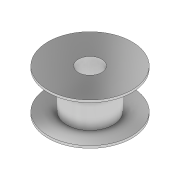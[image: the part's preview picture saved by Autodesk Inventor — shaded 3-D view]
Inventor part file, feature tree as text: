
AUTODESK INVENTOR PART (.ipt)
format: ipt  version: 2020 (Build 240168000, 168)  size: 109,056 bytes
history: native  units: in
note: dims shown in document units (in); Inventor stores cm internally (conversion verified against a paired STEP export)
features: extrude x3, sketch x3
ambient origin geometry x8: Origin, YZ Plane, XZ Plane, XY Plane, X Axis, Y Axis, Z Axis, Center Point
bodies: Solid1 (feature_tree)
feature tree (6):
  extrude  "Extrusion1"  Depth=0.1969in
  extrude  "Extrusion2"  Depth=0.3937in
  extrude  "Extrusion3"  Depth=0.0197in TaperAngle=0.0deg
  sketch  "Sketch1"  dims[d0=0.7087in d1=0.1969in]
  sketch  "Sketch2"  dims[d2=0.0197in d3=0.0in d4=0.3937in]
  sketch  "Sketch3"  dims[d5=0.315in d6=0.0in d7=0.0197in d8=0.0in]
